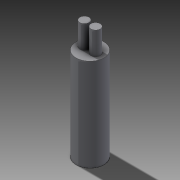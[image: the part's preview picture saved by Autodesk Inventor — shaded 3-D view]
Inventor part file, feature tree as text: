
AUTODESK INVENTOR PART (.ipt)
format: ipt  version: 2014 (Build 180170000, 170)  size: 82,432 bytes
history: native  units: mm
features: extrude x2, sketch x2, reference x1
ambient origin geometry x8: Origin, YZ Plane, XZ Plane, XY Plane, X Axis, Y Axis, Z Axis, Center Point
bodies: Solid1 (feature_tree), Solid2 (feature_tree)
feature tree (5):
  extrude  "Extrusion1"  Depth=20.0mm
  extrude  "Extrusion2"  Depth=5.0mm
  sketch  "Sketch1"  dims[d0=20.0mm d1=0.0mm d2=2.0mm]
  reference  "Reference1"
  sketch  "Sketch2"  dims[d3=2.0mm d4=1.2mm d5=1.2mm d6=5.0mm d7=0.0mm]
